# Revit family: KEUCO_14952010100
name_source: partatom
category: Sonderausstattung
revit_build: Autodesk Revit 2016 (Build: 20150220_1215(x64)
units: mm (PartAtom-declared; Revit-internal decimal feet)

## family parameters
Arbeitsebenenbasiert = Nein
Beim Laden mit Abzugskörper schneiden = Nein
Bemaßung runder Anschluss = Durchmesser verwenden
Gemeinsam genutzt = Nein
Immer vertikal = Ja
Raumberechnungspunkt = Nein
Teiletyp = Normal

## types (3) — shared parameters
Beschreibung = Standmodell, mit Kunststoffeinsatz und Pumpe
Füllmenge: ca. 250 ml
Dosiermenge: ca. 0,5 ml/Hub
Gewicht = 382
Hersteller = KEUCO
Kategorie = ACC
Preisgruppe = 1
Serie = Plan
URL = https://www.keuco.com
Verwendung = BI / GWC / WP

## per-type parameters (varying)
| type | Ausschreibungstext |
| 14952010100 | KEUCO PLAN Lotionspender 14952010100 
Hochglanzverchromter Lotionspender, Standmodell 
in ästhetischem, funktionalem Design
komplett mit herausnehmbarem Kunststoffeinsatz
für leichtes Reinigen und leichtes Befüllen
hochwertige und langlebige Pumpe
Füllmenge ca. 250 ml, für handelsübliche Flüssigseifen
Dosiermenge ca. 0,5 ml/Hub
Grundkörperdurchmesser 65 mm, Höhe 178 mm, Ausladung 96 mm |
| 14952070100 | KEUCO PLAN Lotionspender 14952070100 
Lotionspender aus hochwertigem Edelstahl, Standmodell
in ästhetischem, funktionalem Design
komplett mit herausnehmbarem Kunststoffeinsatz
für leichtes Reinigen und leichtes Befüllen
hochwertige und langlebige Pumpe
Füllmenge ca. 250 ml, für handelsübliche Flüssigseifen
Dosiermenge ca. 0,5 ml /Hub
Grundkörperdurchmesser 65 mm, Höhe 178 mm, Ausladung 96 mm |
| 14952170100 | KEUCO PLAN Lotionspender 14952170100 
Lotionspender aus silber-eloxiertem Aluminium (E6 EV1), 
Stanmodell, in ästhetischem, funktionalem Design
Standmodell, komplett mit herausnehmbarem Kunststoffeinsatz 
für leichtes Reinigen und leichtes Befüllen
hochwertige und langlebige Pumpe
Füllmenge ca. 250 ml, für handelsübliche Flüssigseifen
Dosiermenge ca. 0,5 ml/Hub
Grundkörperdurchmesser 65 mm, Höhe 178 mm, Ausladung 96 mm |

note: column(s) folded — value = type name in every type: Artikelnummer

## geometry (parser evidence)
native form markers: Blend x2, Sweep x3
no freeform markers — native parametric forms only
